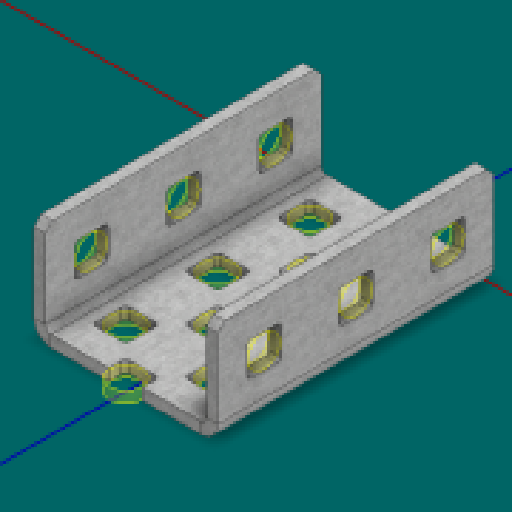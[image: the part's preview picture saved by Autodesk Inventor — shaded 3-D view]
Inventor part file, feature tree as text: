
AUTODESK INVENTOR PART (.ipt)
format: ipt  version: 2025 (Build 290162000, 162)  size: 419,840 bytes
history: native  units: in
note: dims shown in document units (in); Inventor stores cm internally (conversion verified against a paired STEP export)
features: other x36, sketch x5, sheet_metal_op x1
ambient origin geometry x8: Origin, YZ Plane, XZ Plane, XY Plane, X Axis, Y Axis, Z Axis, Center Point
bodies: Solid1 (feature_tree)
feature tree (42):
  other  "Alu C 1x2x1x3.ipt"
  other  "Solid1::Alu C 1x2x1x3.ipt"
  other  "TaggingFeature1"
  sketch  "Sketch1"  dims[d0=0.3937in]
  sketch  "Sketch2"  dims[d1=0.0625in]
  sketch  "Sketch3"
  other  "Flange Pattern Sketch"
  sketch  "Sketch9"
  sheet_metal_op  "Body Pattern Sketch"
  other  "Arc Length"
  sketch  "Sketch14"
  other  "Flange Pattern Plane"
  other  "Srf1"
  other  "Srf2"
  other  "Srf3"
  other  "Srf4"
  other  "Srf5"
  other  "Srf6"
  other  "Srf7"
  other  "Srf8"
  other  "Srf9"
  other  "Srf10"
  other  "Srf11"
  other  "Srf12"
  other  "Srf13"
  other  "Srf14"
  other  "Srf15"
  other  "Srf1::Derived"
  other  "Srf2::Derived"
  other  "Srf823::Derived"
  other  "Srf824::Derived"
  other  "Srf825::Derived"
  other  "Srf826::Derived"
  other  "Srf91::Derived"
  other  "Srf92::Derived"
  other  "Srf856::Derived"
  other  "Srf857::Derived"
  other  "Srf858::Derived"
  other  "Srf859::Derived"
  other  "Srf786::Derived"
  other  "Srf889::Derived"
  other  "Srf890::Derived"
